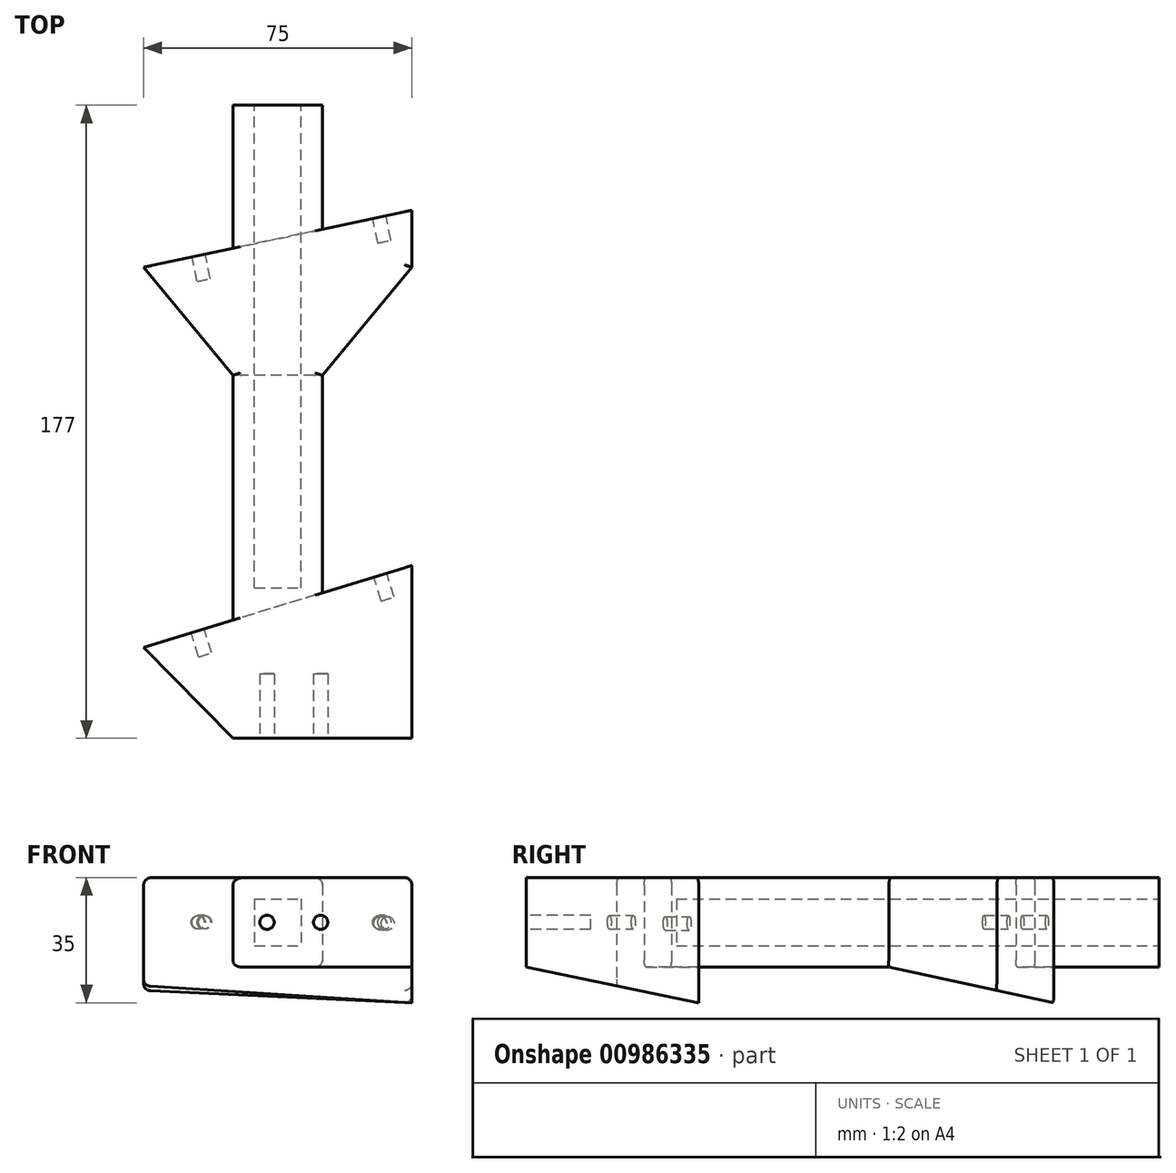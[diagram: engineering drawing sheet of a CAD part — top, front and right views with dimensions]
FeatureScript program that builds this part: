
annotation { "Feature Type Name" : "Feature", "Feature Type Description" : "" }
export const myFeature = defineFeature(function(context is Context, id is Id, definition is map)
    precondition{}
    {
        {
            var Q0;
            Q0=qCreatedBy(makeId("Top.planeOp"),FACE);
            var sketch = newSketch(context, id + "F0", { "sketchPlane" : qUnion([Q0])});
            skLineSegment(sketch, "E0.bottom", {"start": v(0, 0) * mm, "end": v(50, 0) * mm});
            skLineSegment(sketch, "E0.top", {"start": v(0, 33) * mm, "end": v(50, 33) * mm});
            skLineSegment(sketch, "E0.left", {"start": v(0, 0) * mm, "end": v(0, 33) * mm});
            skLineSegment(sketch, "E0.right", {"start": v(50, 0) * mm, "end": v(50, 33) * mm});
            skLineSegment(sketch, "E1", {"start": v(0, 33) * mm, "end": v(50, 48.29) * mm});
            skLineSegment(sketch, "E2", {"start": v(50, 33) * mm, "end": v(50, 48.29) * mm});
            skLineSegment(sketch, "E3", {"start": v(0, 33) * mm, "end": v(-25, 25.36) * mm});
            skLineSegment(sketch, "E4", {"start": v(-25, 25.36) * mm, "end": v(0, 0) * mm});
            skLineSegment(sketch, "E5", {"start": v(0, 33) * mm, "end": v(0, 137) * mm});
            skLineSegment(sketch, "E6", {"start": v(0, 137) * mm, "end": v(25, 137) * mm});
            skLineSegment(sketch, "E7", {"start": v(25, 137) * mm, "end": v(25, 0) * mm});
            skLineSegment(sketch, "E8", {"start": v(0, 137) * mm, "end": v(-25, 131.69) * mm});
            skLineSegment(sketch, "E9", {"start": v(-25, 131.69) * mm, "end": v(-25, 92.43) * mm});
            skLineSegment(sketch, "E10", {"start": v(-25, 131.69) * mm, "end": v(0, 101.46) * mm});
            skLineSegment(sketch, "E11", {"start": v(0, 137) * mm, "end": v(50, 147.63) * mm});
            skLineSegment(sketch, "E12", {"start": v(50, 147.63) * mm, "end": v(50, 131.69) * mm});
            skLineSegment(sketch, "E13", {"start": v(25, 101.46) * mm, "end": v(50, 131.69) * mm});
            skLineSegment(sketch, "E14", {"start": v(0, 137) * mm, "end": v(0, 177) * mm});
            skLineSegment(sketch, "E15", {"start": v(0, 177) * mm, "end": v(25, 177) * mm});
            skPoint(sketch, "E15.endSnap0", {"position": v(25, 142.31) * mm});
            skLineSegment(sketch, "E16", {"start": v(25, 177) * mm, "end": v(25, 137) * mm});
            skSolve(sketch);
        }
        {
            var Q0;
            Q0=qSketchRegion(id+"F0",true);
            extrude(context, id + "F1", {"entities" : qUnion([Q0]), "depth" : 25 * mm});
        }
        {
            var Q0;
            Q0=makeQuery(id+"F1.opExtrude","CAP_FACE",FACE,{"disambiguationData":[OSD([sQuery(id+"F0.wireOp",EDGE,"E0.bottom"),sQuery(id+"F0.wireOp",EDGE,"E0.right"),sQuery(id+"F0.wireOp",EDGE,"E1"),sQuery(id+"F0.wireOp",EDGE,"E2"),sQuery(id+"F0.wireOp",EDGE,"E3"),sQuery(id+"F0.wireOp",EDGE,"E4"),sQuery(id+"F0.wireOp",EDGE,"E5"),sQuery(id+"F0.wireOp",EDGE,"E7"),sQuery(id+"F0.wireOp",EDGE,"E8"),sQuery(id+"F0.wireOp",EDGE,"E10"),sQuery(id+"F0.wireOp",EDGE,"E11"),sQuery(id+"F0.wireOp",EDGE,"E12"),sQuery(id+"F0.wireOp",EDGE,"E13"),sQuery(id+"F0.wireOp",EDGE,"E14"),sQuery(id+"F0.wireOp",EDGE,"E15"),sQuery(id+"F0.wireOp",EDGE,"E16")])],"isStart":true});
            var sketch = newSketch(context, id + "F2", { "sketchPlane" : qUnion([Q0])});
            skLineSegment(sketch, "E17", {"start": v(25, -101.46) * mm, "end": v(0, -101.46) * mm});
            skLineSegment(sketch, "E18", {"start": v(0, -101.46) * mm, "end": v(-25, -131.69) * mm});
            skLineSegment(sketch, "E19", {"start": v(-25, -131.69) * mm, "end": v(50, -147.63) * mm});
            skLineSegment(sketch, "E20", {"start": v(50, -147.63) * mm, "end": v(50, -131.69) * mm});
            skLineSegment(sketch, "E21", {"start": v(50, -131.69) * mm, "end": v(25, -101.46) * mm});
            skSolve(sketch);
        }
        {
            var Q0;
            Q0=qSketchRegion(id+"F2",true);
            extrude(context, id + "F3", {"entities" : qUnion([Q0]), "operationType" : NewBodyOperationType.ADD, "depth" : 10 * mm});
        }
        {
            var Q0;
            Q0=makeQuery(id+"F1.opExtrude","SWEPT_FACE",FACE,{"disambiguationData":[OSD([sQuery(id+"F0.wireOp",EDGE,"E7")])]});
            var sketch = newSketch(context, id + "F4", { "sketchPlane" : qUnion([Q0])});
            skLineSegment(sketch, "E22", {"start": v(147.63, -10) * mm, "end": v(101.46, 0) * mm});
            skLineSegment(sketch, "E23", {"start": v(101.46, 0) * mm, "end": v(101.46, -21.14) * mm});
            skLineSegment(sketch, "E24", {"start": v(101.46, -21.14) * mm, "end": v(147.63, -10) * mm});
            skSolve(sketch);
        }
        {
            var Q0;
            Q0=qSketchRegion(id+"F4",true);
            extrude(context, id + "F5", {"entities" : qUnion([Q0]), "operationType" : NewBodyOperationType.REMOVE, "oppositeDirection" : true, "depth" : 163.4 * mm, "symmetric" : true});
        }
        {
            var Q0;
            {var subQ0=sQuery(id+"F0.wireOp",EDGE,"E13");var subQ1=sQuery(id+"F0.wireOp",EDGE,"E7");var subQ2=sQuery(id+"F0.wireOp",EDGE,"E5");var subQ3=sQuery(id+"F0.wireOp",EDGE,"E4");var subQ4=sQuery(id+"F0.wireOp",EDGE,"E0.bottom");var subQ5=sQuery(id+"F0.wireOp",EDGE,"E10");var subQ6=sQuery(id+"F0.wireOp",EDGE,"E2");var subQ7=sQuery(id+"F0.wireOp",EDGE,"E0.right");var subQ8=sQuery(id+"F0.wireOp",EDGE,"E1");var subQ9=sQuery(id+"F0.wireOp",EDGE,"E3");Q0=makeQuery(id+"F3.boolean.opBoolean","SPLIT",FACE,{"disambiguationData":[TD([makeQuery(id+"F1.opExtrude","SWEPT_FACE",FACE,{"disambiguationData":[OSD([subQ4])]})])],"derivedFrom":makeQuery(id+"F1.opExtrude","CAP_FACE",FACE,{"disambiguationData":[OSD([subQ4,subQ7,subQ8,subQ6,subQ9,subQ3,subQ2,subQ1,sQuery(id+"F0.wireOp",EDGE,"E8"),subQ5,sQuery(id+"F0.wireOp",EDGE,"E11"),sQuery(id+"F0.wireOp",EDGE,"E12"),subQ0,sQuery(id+"F0.wireOp",EDGE,"E14"),sQuery(id+"F0.wireOp",EDGE,"E15"),sQuery(id+"F0.wireOp",EDGE,"E16")])],"isStart":true})});}
            var sketch = newSketch(context, id + "F6", { "sketchPlane" : qUnion([Q0])});
            skLineSegment(sketch, "E25", {"start": v(50, 0) * mm, "end": v(50, -48.29) * mm});
            skLineSegment(sketch, "E26", {"start": v(50, -48.29) * mm, "end": v(-25, -25.36) * mm});
            skLineSegment(sketch, "E27", {"start": v(-25, -25.36) * mm, "end": v(0, 0) * mm});
            skLineSegment(sketch, "E28", {"start": v(0, 0) * mm, "end": v(50, 0) * mm});
            skSolve(sketch);
        }
        {
            var Q0;
            Q0=qSketchRegion(id+"F6",true);
            extrude(context, id + "F7", {"entities" : qUnion([Q0]), "operationType" : NewBodyOperationType.ADD, "depth" : 10 * mm});
        }
        {
            var Q0;
            Q0=makeQuery(id+"F7.boolean.opBoolean","MERGE",FACE,{"derivedFrom":[makeQuery(id+"F1.opExtrude","SWEPT_FACE",FACE,{"disambiguationData":[OSD([sQuery(id+"F0.wireOp",EDGE,"E0.right"),sQuery(id+"F0.wireOp",EDGE,"E2")])]}),makeQuery(id+"F7.opExtrude","SWEPT_FACE",FACE,{"disambiguationData":[OSD([sQuery(id+"F6.wireOp",EDGE,"E25")])]})]});
            var sketch = newSketch(context, id + "F8", { "sketchPlane" : qUnion([Q0])});
            skLineSegment(sketch, "E29", {"start": v(0, 0) * mm, "end": v(48.29, -10) * mm});
            skLineSegment(sketch, "E30", {"start": v(48.29, -10) * mm, "end": v(48.29, -39.53) * mm});
            skLineSegment(sketch, "E31", {"start": v(48.29, -39.53) * mm, "end": v(0, -39.53) * mm});
            skLineSegment(sketch, "E32", {"start": v(0, -39.53) * mm, "end": v(0, 0) * mm});
            skSolve(sketch);
        }
        {
            var Q0;
            Q0=qSketchRegion(id+"F8",true);
            extrude(context, id + "F9", {"entities" : qUnion([Q0]), "operationType" : NewBodyOperationType.REMOVE, "oppositeDirection" : true, "depth" : 92 * mm});
        }
        {
            var Q0;
            Q0=makeQuery(id+"F1.opExtrude","SWEPT_FACE",FACE,{"disambiguationData":[OSD([sQuery(id+"F0.wireOp",EDGE,"E15")])]});
            var sketch = newSketch(context, id + "F10", { "sketchPlane" : qUnion([Q0])});
            skLineSegment(sketch, "E33.bottom", {"start": v(-6, 19) * mm, "end": v(-19, 19) * mm});
            skLineSegment(sketch, "E33.top", {"start": v(-6, 6) * mm, "end": v(-19, 6) * mm});
            skLineSegment(sketch, "E33.left", {"start": v(-6, 19) * mm, "end": v(-6, 6) * mm});
            skLineSegment(sketch, "E33.right", {"start": v(-19, 19) * mm, "end": v(-19, 6) * mm});
            skPoint(sketch, "E33.middle", {"position": v(-12.5, 12.5) * mm});
            skPoint(sketch, "E33.middle.positionSnap0", {"position": v(-25, 12.5) * mm});
            skPoint(sketch, "E33.middle.positionSnap1", {"position": v(-12.5, 25) * mm});
            skPoint(sketch, "E33.centerSnap0", {"position": v(-25, 12.5) * mm});
            skPoint(sketch, "E33.centerSnap1", {"position": v(-12.5, 25) * mm});
            skSolve(sketch);
        }
        {
            var Q0;
            Q0=qSketchRegion(id+"F10",true);
            extrude(context, id + "F11", {"entities" : qUnion([Q0]), "operationType" : NewBodyOperationType.REMOVE, "oppositeDirection" : true, "depth" : 135 * mm});
        }
        {
            var Q0;
            Q0=makeQuery(id+"F3.boolean.opBoolean","MERGE",FACE,{"derivedFrom":[makeQuery(id+"F1.opExtrude","SWEPT_FACE",FACE,{"disambiguationData":[OSD([sQuery(id+"F0.wireOp",EDGE,"E8")])]}),makeQuery(id+"F1.opExtrude","SWEPT_FACE",FACE,{"disambiguationData":[OSD([sQuery(id+"F0.wireOp",EDGE,"E11")])]}),makeQuery(id+"F3.opExtrude","SWEPT_FACE",FACE,{"disambiguationData":[OSD([sQuery(id+"F2.wireOp",EDGE,"E19")])]})]});
            var sketch = newSketch(context, id + "F12", { "sketchPlane" : qUnion([Q0])});
            skLineSegment(sketch, "E34", {"start": v(-2.93, 25) * mm, "end": v(-2.93, 12.5) * mm});
            skPoint(sketch, "E34.endSnap0", {"position": v(-28.48, 12.5) * mm});
            skLineSegment(sketch, "E35", {"start": v(-2.93, 12.5) * mm, "end": v(-18.63, 12.5) * mm});
            skCircle(sketch, "E36", {"center": v(-18.63, 12.5) * mm, "radius": 1.9 * mm});
            skLineSegment(sketch, "E37", {"start": v(-79.6, 25) * mm, "end": v(-79.6, 12.5) * mm});
            skLineSegment(sketch, "E38", {"start": v(-79.6, 12.5) * mm, "end": v(-70.3, 12.5) * mm});
            skCircle(sketch, "E39", {"center": v(-70.3, 12.5) * mm, "radius": 1.9 * mm});
            skSolve(sketch);
        }
        {
            var Q0;
            Q0=qSketchRegion(id+"F12",true);
            extrude(context, id + "F13", {"entities" : qUnion([Q0]), "operationType" : NewBodyOperationType.REMOVE, "oppositeDirection" : true, "depth" : 7 * mm});
        }
        {
            var Q0;
            Q0=makeQuery(id+"F7.boolean.opBoolean","MERGE",FACE,{"derivedFrom":[makeQuery(id+"F1.opExtrude","SWEPT_FACE",FACE,{"disambiguationData":[OSD([sQuery(id+"F0.wireOp",EDGE,"E1")])]}),makeQuery(id+"F1.opExtrude","SWEPT_FACE",FACE,{"disambiguationData":[OSD([sQuery(id+"F0.wireOp",EDGE,"E3")])]}),makeQuery(id+"F7.opExtrude","SWEPT_FACE",FACE,{"disambiguationData":[OSD([sQuery(id+"F6.wireOp",EDGE,"E26")])]})]});
            var sketch = newSketch(context, id + "F14", { "sketchPlane" : qUnion([Q0])});
            skLineSegment(sketch, "E40", {"start": v(16.5, 25) * mm, "end": v(16.5, 12.5) * mm});
            skPoint(sketch, "E40.endSnap0", {"position": v(-9.65, 12.5) * mm});
            skLineSegment(sketch, "E41", {"start": v(16.5, 12.5) * mm, "end": v(0.7, 12.5) * mm});
            skCircle(sketch, "E42", {"center": v(0.7, 12.5) * mm, "radius": 1.9 * mm});
            skLineSegment(sketch, "E43", {"start": v(-61.93, 25) * mm, "end": v(-61.93, 12.5) * mm});
            skLineSegment(sketch, "E44", {"start": v(-61.93, 12.5) * mm, "end": v(-52.74, 12.22) * mm});
            skCircle(sketch, "E45", {"center": v(-52.74, 12.22) * mm, "radius": 1.9 * mm});
            skSolve(sketch);
        }
        {
            var Q0;
            Q0=qSketchRegion(id+"F14",true);
            extrude(context, id + "F15", {"entities" : qUnion([Q0]), "operationType" : NewBodyOperationType.REMOVE, "oppositeDirection" : true, "depth" : 7 * mm});
        }
        {
            var Q0;
            Q0=makeQuery(id+"F7.boolean.opBoolean","MERGE",FACE,{"derivedFrom":[makeQuery(id+"F1.opExtrude","SWEPT_FACE",FACE,{"disambiguationData":[OSD([sQuery(id+"F0.wireOp",EDGE,"E0.bottom")])]}),makeQuery(id+"F7.opExtrude","SWEPT_FACE",FACE,{"disambiguationData":[OSD([sQuery(id+"F6.wireOp",EDGE,"E28")])]})]});
            var sketch = newSketch(context, id + "F16", { "sketchPlane" : qUnion([Q0])});
            skLineSegment(sketch, "E46", {"start": v(0, 12.5) * mm, "end": v(9.5, 12.5) * mm});
            skLineSegment(sketch, "E47", {"start": v(9.5, 12.5) * mm, "end": v(24.5, 12.5) * mm});
            skCircle(sketch, "E48", {"center": v(9.5, 12.5) * mm, "radius": 2 * mm});
            skCircle(sketch, "E49", {"center": v(24.5, 12.5) * mm, "radius": 2 * mm});
            skSolve(sketch);
        }
        {
            var Q0;
            Q0=qSketchRegion(id+"F16",true);
            extrude(context, id + "F17", {"entities" : qUnion([Q0]), "operationType" : NewBodyOperationType.REMOVE, "oppositeDirection" : true, "depth" : 18 * mm});
        }
        {
            var Q0;
            Q0=makeQuery(id+"F1.opExtrude","CAP_EDGE",EDGE,{"disambiguationData":[OSD([sQuery(id+"F0.wireOp",EDGE,"E13")])],"isStart":false});
            var Q1;
            Q1=makeQuery(id+"F5.boolean.opBoolean","INTERSECT",EDGE,{"derivedFrom":[makeQuery(id+"F3.boolean.opBoolean","MERGE",FACE,{"derivedFrom":[makeQuery(id+"F1.opExtrude","SWEPT_FACE",FACE,{"disambiguationData":[OSD([sQuery(id+"F0.wireOp",EDGE,"E13")])]}),makeQuery(id+"F3.opExtrude","SWEPT_FACE",FACE,{"disambiguationData":[OSD([sQuery(id+"F2.wireOp",EDGE,"E21")])]})]}),makeQuery(id+"F5.opExtrude","SWEPT_FACE",FACE,{"disambiguationData":[OSD([sQuery(id+"F4.wireOp",EDGE,"E22")])]})]});
            var Q2;
            Q2=makeQuery(id+"F5.boolean.opBoolean","INTERSECT",EDGE,{"derivedFrom":[makeQuery(id+"F3.boolean.opBoolean","MERGE",FACE,{"derivedFrom":[makeQuery(id+"F1.opExtrude","SWEPT_FACE",FACE,{"disambiguationData":[OSD([sQuery(id+"F0.wireOp",EDGE,"E12")])]}),makeQuery(id+"F3.opExtrude","SWEPT_FACE",FACE,{"disambiguationData":[OSD([sQuery(id+"F2.wireOp",EDGE,"E20")])]})]}),makeQuery(id+"F5.opExtrude","SWEPT_FACE",FACE,{"disambiguationData":[OSD([sQuery(id+"F4.wireOp",EDGE,"E22")])]})]});
            var Q3;
            Q3=makeQuery(id+"F1.opExtrude","CAP_EDGE",EDGE,{"disambiguationData":[OSD([sQuery(id+"F0.wireOp",EDGE,"E12")])],"isStart":false});
            var Q4;
            Q4=makeQuery(id+"F5.boolean.opBoolean","INTERSECT",EDGE,{"derivedFrom":[makeQuery(id+"F3.boolean.opBoolean","MERGE",FACE,{"derivedFrom":[makeQuery(id+"F1.opExtrude","SWEPT_FACE",FACE,{"disambiguationData":[OSD([sQuery(id+"F0.wireOp",EDGE,"E10")])]}),makeQuery(id+"F3.opExtrude","SWEPT_FACE",FACE,{"disambiguationData":[OSD([sQuery(id+"F2.wireOp",EDGE,"E18")])]})]}),makeQuery(id+"F5.opExtrude","SWEPT_FACE",FACE,{"disambiguationData":[OSD([sQuery(id+"F4.wireOp",EDGE,"E22")])]})]});
            var Q5;
            Q5=makeQuery(id+"F1.opExtrude","CAP_EDGE",EDGE,{"disambiguationData":[OSD([sQuery(id+"F0.wireOp",EDGE,"E10")])],"isStart":false});
            var Q6;
            Q6=makeQuery(id+"F1.opExtrude","CAP_EDGE",EDGE,{"disambiguationData":[OSD([sQuery(id+"F0.wireOp",EDGE,"E7")])],"isStart":true});
            var Q7;
            Q7=makeQuery(id+"F1.opExtrude","CAP_EDGE",EDGE,{"disambiguationData":[OSD([sQuery(id+"F0.wireOp",EDGE,"E7")])],"isStart":false});
            var Q8;
            Q8=makeQuery(id+"F1.opExtrude","CAP_EDGE",EDGE,{"disambiguationData":[OSD([sQuery(id+"F0.wireOp",EDGE,"E5")])],"isStart":true});
            var Q9;
            Q9=makeQuery(id+"F1.opExtrude","CAP_EDGE",EDGE,{"disambiguationData":[OSD([sQuery(id+"F0.wireOp",EDGE,"E5")])],"isStart":false});
            var Q10;
            Q10=makeQuery(id+"F9.boolean.opBoolean","COPY",EDGE,{"derivedFrom":makeQuery(id+"F9.opExtrude","CAP_EDGE",EDGE,{"disambiguationData":[OSD([sQuery(id+"F8.wireOp",EDGE,"E29")])],"isStart":true})});
            var Q11;
            Q11=makeQuery(id+"F1.opExtrude","CAP_EDGE",EDGE,{"disambiguationData":[OSD([sQuery(id+"F0.wireOp",EDGE,"E0.right"),sQuery(id+"F0.wireOp",EDGE,"E2")])],"isStart":false});
            var Q12;
            Q12=makeQuery(id+"F1.opExtrude","CAP_EDGE",EDGE,{"disambiguationData":[OSD([sQuery(id+"F0.wireOp",EDGE,"E4")])],"isStart":false});
            var Q13;
            Q13=makeQuery(id+"F9.boolean.opBoolean","INTERSECT",EDGE,{"derivedFrom":[makeQuery(id+"F7.boolean.opBoolean","MERGE",FACE,{"derivedFrom":[makeQuery(id+"F1.opExtrude","SWEPT_FACE",FACE,{"disambiguationData":[OSD([sQuery(id+"F0.wireOp",EDGE,"E4")])]}),makeQuery(id+"F7.opExtrude","SWEPT_FACE",FACE,{"disambiguationData":[OSD([sQuery(id+"F6.wireOp",EDGE,"E27")])]})]}),makeQuery(id+"F9.opExtrude","SWEPT_FACE",FACE,{"disambiguationData":[OSD([sQuery(id+"F8.wireOp",EDGE,"E29")])]})]});
            var Q14;
            Q14=makeQuery(id+"F1.opExtrude","CAP_EDGE",EDGE,{"disambiguationData":[OSD([sQuery(id+"F0.wireOp",EDGE,"E14")])],"isStart":true});
            var Q15;
            Q15=makeQuery(id+"F1.opExtrude","CAP_EDGE",EDGE,{"disambiguationData":[OSD([sQuery(id+"F0.wireOp",EDGE,"E14")])],"isStart":false});
            var Q16;
            Q16=makeQuery(id+"F1.opExtrude","CAP_EDGE",EDGE,{"disambiguationData":[OSD([sQuery(id+"F0.wireOp",EDGE,"E16")])],"isStart":false});
            var Q17;
            Q17=makeQuery(id+"F1.opExtrude","CAP_EDGE",EDGE,{"disambiguationData":[OSD([sQuery(id+"F0.wireOp",EDGE,"E16")])],"isStart":true});
            fillet(context, id + "F18", {"entities" : qUnion([Q0, Q1, Q2, Q3, Q4, Q5, Q6, Q7, Q8, Q9, Q10, Q11, Q12, Q13, Q14, Q15, Q16, Q17]), "radius" : 2 * mm, "tangentPropagation" : true, "allowEdgeOverflow" : false});
        }
    });
